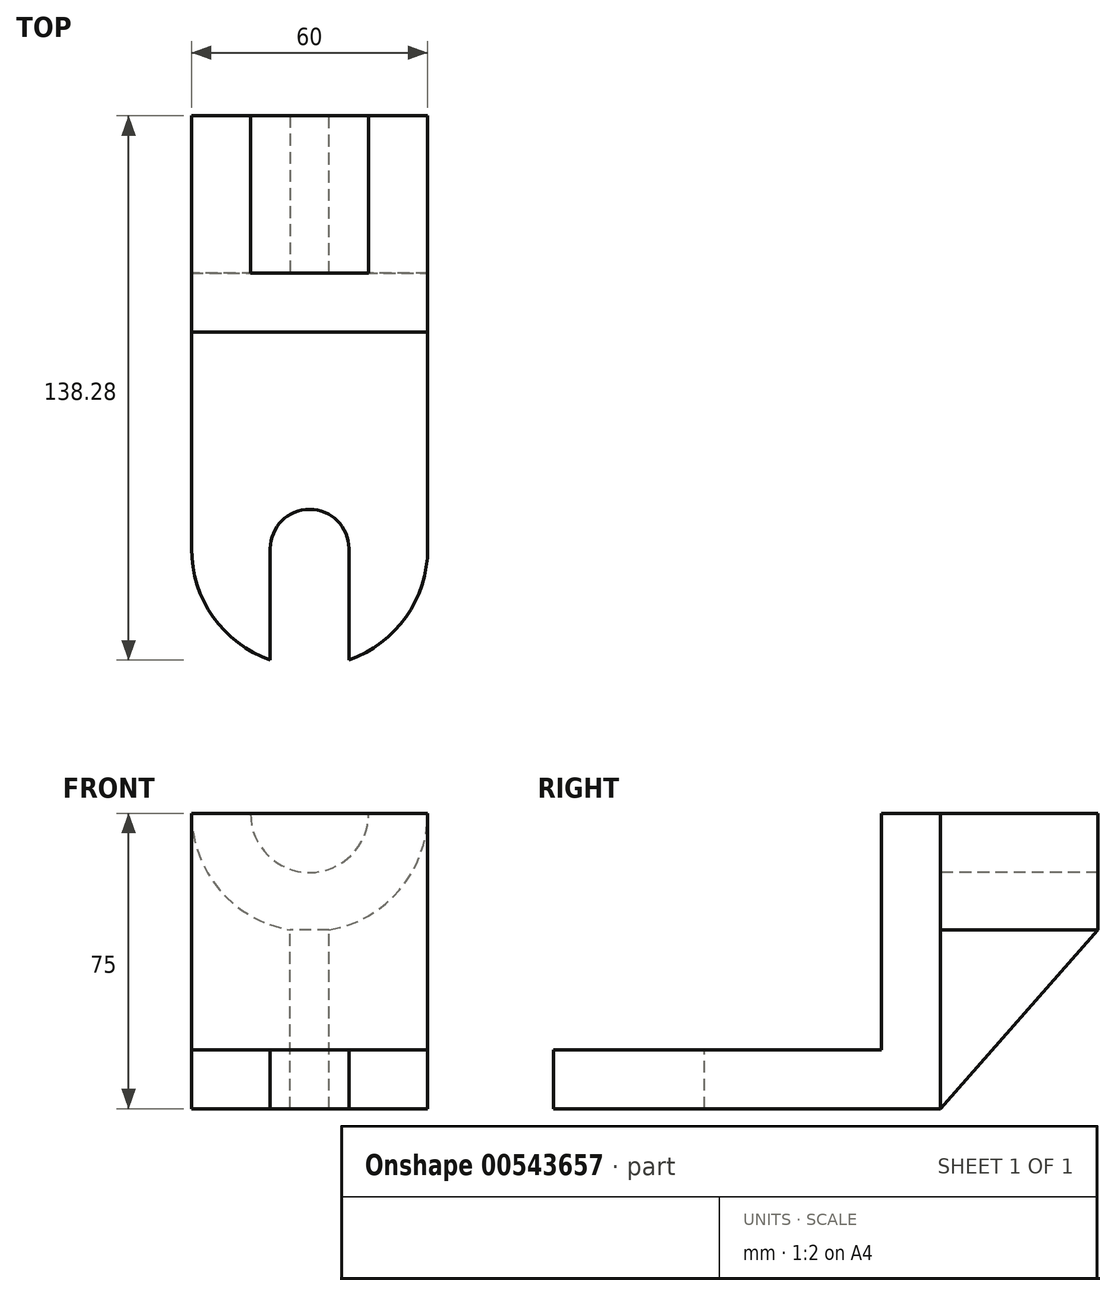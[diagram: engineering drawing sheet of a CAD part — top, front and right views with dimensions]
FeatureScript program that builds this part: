
annotation { "Feature Type Name" : "Feature", "Feature Type Description" : "" }
export const myFeature = defineFeature(function(context is Context, id is Id, definition is map)
    precondition{}
    {
        {
            var Q0;
            Q0=qCreatedBy(makeId("Top.planeOp"),FACE);
            var sketch = newSketch(context, id + "F0", { "sketchPlane" : qUnion([Q0])});
            skLineSegment(sketch, "E0.bottom", {"start": v(-12.4, 40.31) * mm, "end": v(47.6, 40.31) * mm});
            skLineSegment(sketch, "E0.top", {"start": v(-12.4, -29.69) * mm, "end": v(47.6, -29.69) * mm});
            skLineSegment(sketch, "E0.left", {"start": v(-12.4, 40.31) * mm, "end": v(-12.4, -29.69) * mm});
            skLineSegment(sketch, "E0.right", {"start": v(47.6, 40.31) * mm, "end": v(47.6, -29.69) * mm});
            skCircle(sketch, "E1", {"center": v(17.6, -29.69) * mm, "radius": 30 * mm});
            skLineSegment(sketch, "E2", {"start": v(-12.4, 40.31) * mm, "end": v(-12.4, 25.31) * mm});
            skLineSegment(sketch, "E3", {"start": v(-12.4, 25.31) * mm, "end": v(47.6, 25.31) * mm});
            skSolve(sketch);
        }
        {
            var Q0;
            {var subQ0=sQuery(id+"F0.wireOp",EDGE,"E0.bottom");Q0=makeQuery(id+"F0.imprint","IMPRINT",FACE,{"disambiguationData":[TD([[makeQuery(id+"F0.imprint","IMPRINT",EDGE,{"derivedFrom":subQ0}),-1.0]])]});}
            extrude(context, id + "F1", {"entities" : qUnion([Q0]), "depth" : 75 * mm, "offsetDistance" : 25 * mm});
        }
        {
            var Q0;
            Q0 = qSketchRegion(id + "F0", true);
            extrude(context, id + "F2", {"entities" : qUnion([Q0]), "operationType" : NewBodyOperationType.ADD, "depth" : 15 * mm, "offsetDistance" : 25 * mm});
        }
        {
            var Q0;
            Q0=makeQuery(id+"F2.opExtrude","CAP_FACE",FACE,{"disambiguationData":[OSD([sQuery(id+"F0.wireOp",EDGE,"E0.bottom"),sQuery(id+"F0.wireOp",EDGE,"E0.left"),sQuery(id+"F0.wireOp",EDGE,"E0.right"),sQuery(id+"F0.wireOp",EDGE,"E1"),sQuery(id+"F0.wireOp",EDGE,"E2")])],"isStart":false});
            var sketch = newSketch(context, id + "F3", { "sketchPlane" : qUnion([Q0])});
            skLineSegment(sketch, "E4.0.0", {"start": v(47.6, 25.31) * mm, "end": v(-12.4, 25.31) * mm});
            skLineSegment(sketch, "E4.0.1", {"start": v(-12.4, 25.31) * mm, "end": v(-12.4, -29.69) * mm});
            skArc(sketch, "E4.0.2", {"start": v(-12.4, -29.69) * mm, "mid": v(17.6, -59.69) * mm, "end": v(47.6, -29.69) * mm});
            skLineSegment(sketch, "E4.0.3", {"start": v(47.6, -29.69) * mm, "end": v(47.6, 25.31) * mm});
            skCircle(sketch, "E5.0", {"center": v(17.6, -29.69) * mm, "radius": 30 * mm});
            skLineSegment(sketch, "E6", {"start": v(17.6, -29.69) * mm, "end": v(7.6, -29.69) * mm});
            skLineSegment(sketch, "E7", {"start": v(7.6, -29.69) * mm, "end": v(27.6, -29.69) * mm});
            skLineSegment(sketch, "E8", {"start": v(7.6, -29.69) * mm, "end": v(7.6, -57.97) * mm});
            skLineSegment(sketch, "E9", {"start": v(27.6, -29.69) * mm, "end": v(27.6, -57.97) * mm});
            skCircle(sketch, "E10", {"center": v(17.6, -29.69) * mm, "radius": 10 * mm});
            skSolve(sketch);
        }
        {
            var Q0;
            {var subQ0=sQuery(id+"F3.wireOp",EDGE,"E8");Q0=makeQuery(id+"F3.imprint","IMPRINT",FACE,{"disambiguationData":[TD([[makeQuery(id+"F3.imprint","IMPRINT",EDGE,{"derivedFrom":subQ0}),1.0]])]});}
            var Q1;
            {var subQ1=sQuery(id+"F3.wireOp",EDGE,"E7");var subQ3=makeQuery(id+"F3.imprint","IMPRINT",VERTEX,{"derivedFrom":subQ1});Q1=makeQuery(id+"F3.imprint","IMPRINT",FACE,{"disambiguationData":[TD([[makeQuery(id+"F3.imprint","IMPRINT",EDGE,{"disambiguationData":[TD([[subQ3,1.0]])],"derivedFrom":subQ1}),-1.0]])]});}
            var Q2;
            {var subQ1=sQuery(id+"F3.wireOp",EDGE,"E7");var subQ3=makeQuery(id+"F3.imprint","IMPRINT",VERTEX,{"derivedFrom":subQ1});Q2=makeQuery(id+"F3.imprint","IMPRINT",FACE,{"disambiguationData":[TD([[makeQuery(id+"F3.imprint","IMPRINT",EDGE,{"disambiguationData":[TD([[subQ3,1.0]])],"derivedFrom":subQ1}),1.0]])]});}
            extrude(context, id + "F4", {"entities" : qUnion([Q0, Q1, Q2]), "operationType" : NewBodyOperationType.REMOVE, "oppositeDirection" : true, "depth" : 25 * mm, "offsetDistance" : 25 * mm});
        }
        {
            var Q0;
            Q0=makeQuery(id+"F1.opExtrude","SWEPT_FACE",FACE,{"disambiguationData":[OSD([sQuery(id+"F0.wireOp",EDGE,"E0.bottom")])]});
            var sketch = newSketch(context, id + "F5", { "sketchPlane" : qUnion([Q0])});
            skArc(sketch, "E11", {"start": v(-47.6, 75) * mm, "mid": v(-17.6, 45) * mm, "end": v(12.4, 75) * mm});
            skLineSegment(sketch, "E12", {"start": v(-47.6, 75) * mm, "end": v(-42.23, 75) * mm});
            skLineSegment(sketch, "E13", {"start": v(12.4, 75) * mm, "end": v(-47.6, 75) * mm});
            skCircle(sketch, "E14", {"center": v(-17.6, 75) * mm, "radius": 15 * mm});
            skSolve(sketch);
        }
        {
            var Q0;
            {var subQ0=sQuery(id+"F5.wireOp",EDGE,"E11");Q0=makeQuery(id+"F5.imprint","IMPRINT",FACE,{"disambiguationData":[TD([[makeQuery(id+"F5.imprint","IMPRINT",EDGE,{"derivedFrom":subQ0}),1.0]])]});}
            extrude(context, id + "F6", {"entities" : qUnion([Q0]), "operationType" : NewBodyOperationType.ADD, "depth" : 40 * mm, "offsetDistance" : 25 * mm});
        }
        {
            var Q0;
            {var subQ1=sQuery(id+"F0.wireOp",EDGE,"E0.right");var subQ4=sQuery(id+"F0.wireOp",EDGE,"E0.bottom");Q0=makeQuery(id+"F6.boolean.opBoolean","SPLIT",FACE,{"disambiguationData":[TD([makeQuery(id+"F1.opExtrude","SWEPT_FACE",FACE,{"disambiguationData":[OSD([subQ1])]})])],"derivedFrom":makeQuery(id+"F1.opExtrude","SWEPT_FACE",FACE,{"disambiguationData":[OSD([subQ4])]})});}
            var sketch = newSketch(context, id + "F7", { "sketchPlane" : qUnion([Q0])});
            skLineSegment(sketch, "E15", {"start": v(-47.6, 0) * mm, "end": v(-22.6, 0) * mm});
            skLineSegment(sketch, "E16", {"start": v(-22.6, 0) * mm, "end": v(-12.6, 0) * mm});
            skLineSegment(sketch, "E17", {"start": v(-12.6, 0) * mm, "end": v(-12.6, 45.42) * mm});
            skLineSegment(sketch, "E18", {"start": v(-22.6, 0) * mm, "end": v(-22.6, 45.42) * mm});
            skSolve(sketch);
        }
        {
            var Q0;
            Q0=makeQuery(id+"F7.imprint","IMPRINT",FACE,{"disambiguationData":[TD([[makeQuery(id+"F7.imprint","IMPRINT",EDGE,{"derivedFrom":sQuery(id+"F7.wireOp",EDGE,"E16")}),-1.0]])]});
            extrude(context, id + "F8", {"entities" : qUnion([Q0]), "operationType" : NewBodyOperationType.ADD, "depth" : 40 * mm, "offsetDistance" : 25 * mm});
        }
        {
            var Q0;
            Q0=makeQuery(id+"F8.opExtrude","SWEPT_FACE",FACE,{"disambiguationData":[OSD([sQuery(id+"F7.wireOp",EDGE,"E17")])]});
            var sketch = newSketch(context, id + "F9", { "sketchPlane" : qUnion([Q0])});
            skLineSegment(sketch, "E19", {"start": v(-80.31, 45.42) * mm, "end": v(-40.31, 0) * mm});
            skSolve(sketch);
        }
        {
            var Q0;
            Q0=makeQuery(id+"F9.imprint","IMPRINT",FACE,{"disambiguationData":[TD([[makeQuery(id+"F9.imprint","IMPRINT",EDGE,{"derivedFrom":sQuery(id+"F9.wireOp",EDGE,"E19")}),-1.0]])]});
            extrude(context, id + "F10", {"entities" : qUnion([Q0]), "operationType" : NewBodyOperationType.REMOVE, "oppositeDirection" : true, "depth" : 25 * mm, "offsetDistance" : 25 * mm});
        }
    });
